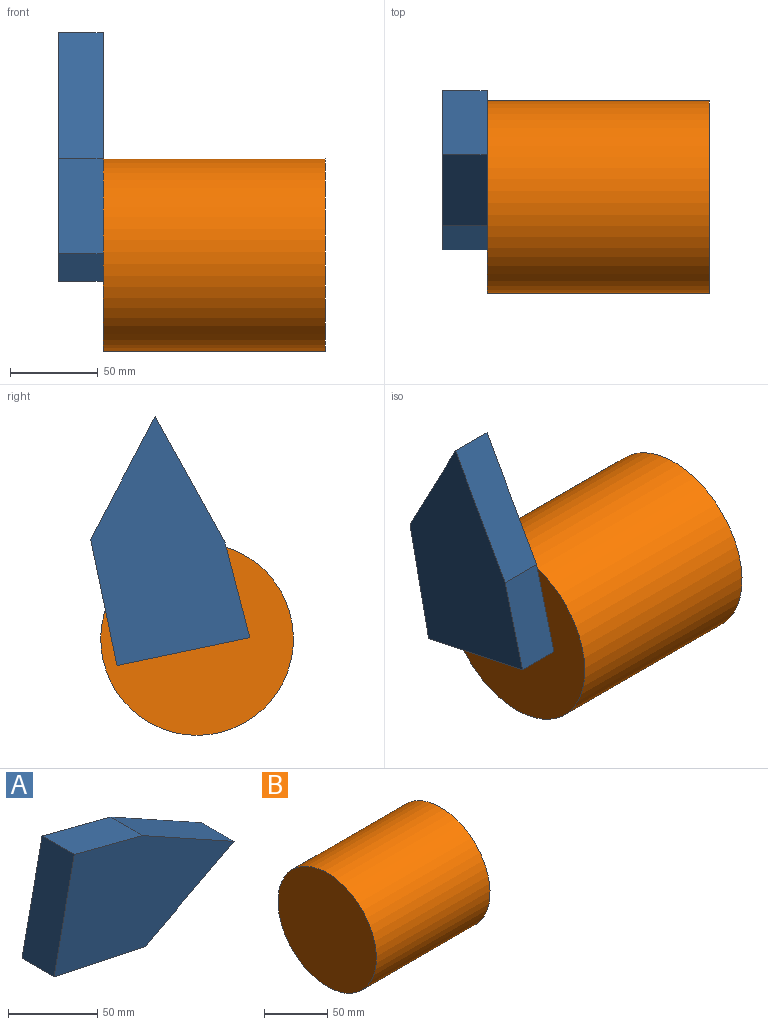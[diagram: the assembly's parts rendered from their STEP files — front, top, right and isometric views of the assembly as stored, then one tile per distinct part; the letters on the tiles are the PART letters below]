
ASSEMBLY  parts=2 mates=1
PART A: 7 faces, bbox 142.1x25.4x90.9 mm
  f0: plane 70.09x36.8mm, normal (0.46,0,-0.89), area 2010.8mm2, adj f1,f4,f5,f6
  f1: plane 72.18x40.05mm, normal (0.49,0,0.87), area 2096.8mm2, adj f0,f2,f5,f6
  f2: plane 54.08x25.4mm, normal (0.25,0,0.97), area 1419.4mm2, adj f1,f3,f5,f6
  f3: plane 75.86x25.4mm, normal (-0.98,0,0.2), area 1968.4mm2, adj f2,f4,f5,f6
  f4: plane 72.04x25.4mm, normal (-0.2,0,-0.98), area 1869.3mm2, adj f0,f3,f5,f6
  f5: plane 142.13x90.92mm, normal (0,-1,0), area 7647.2mm2, adj f0,f1,f2,f3,f4
  f6: plane 142.13x90.92mm, normal (0,1,0), area 7647.2mm2, adj f0,f1,f2,f3,f4
PART B: 3 faces, bbox 127x110.1x110.1 mm
  f0: cylinder r=55.03mm len=127mm, axis (-1,0,0), area 43911mm2, adj f1,f2
  f1: plane 110.06x110.06mm, normal (1,0,0), area 9513.3mm2, adj f0
  f2: plane 110.06x110.06mm, normal (-1,0,0), area 9513.3mm2, adj f0
PLACE A rot(axis=(0.58,-0.58,0.58),120deg) t=(52.81,65.06,160.58)mm
PLACE B t=(141.71,-64.88,-40.36)mm
MATE planar A.f5 <-> B.f0  axis (1,0,0) through (78.21,60.06,77.41)mm
